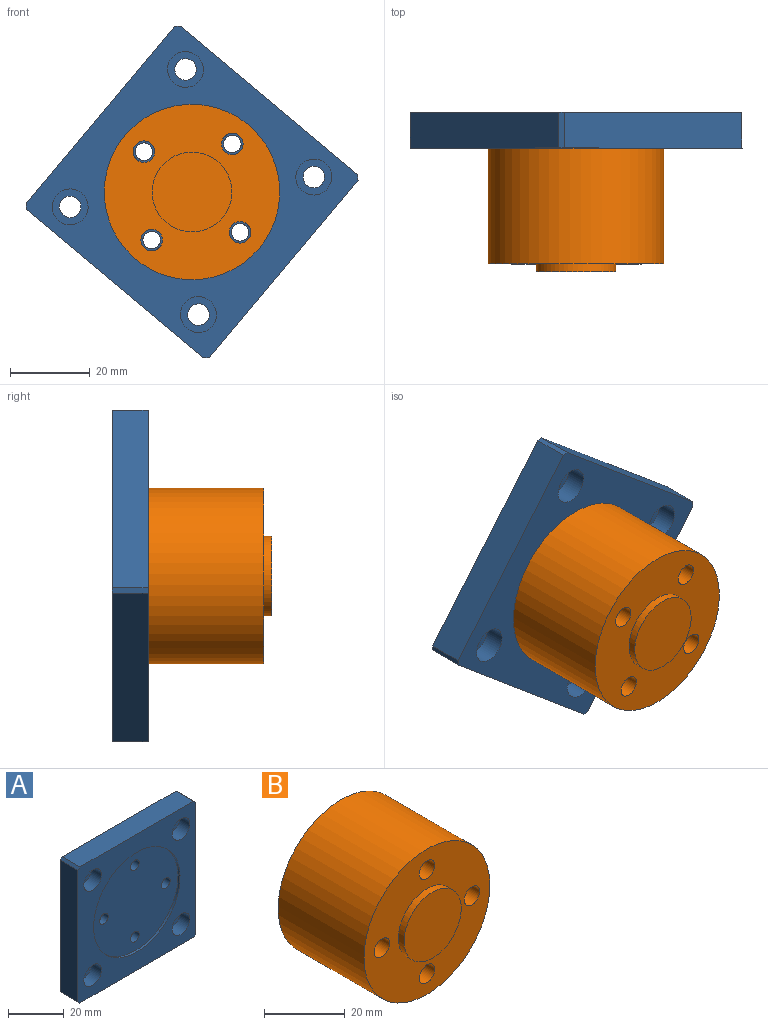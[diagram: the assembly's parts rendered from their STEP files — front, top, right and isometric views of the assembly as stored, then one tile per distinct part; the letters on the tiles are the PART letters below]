
ASSEMBLY  parts=2 mates=1
PART A: 36 faces, bbox 60x9x60 mm
  f0: cylinder r=2.7mm len=5.4mm, axis (0,-1,0), area 64.5mm2, adj f19,f30
  f1: cylinder r=2.7mm len=5.4mm, axis (0,-1,0), area 64.5mm2, adj f19,f28
  f2: cylinder r=2.7mm len=5.4mm, axis (0,-1,0), area 64.5mm2, adj f19,f26
  f3: cylinder r=2.7mm len=5.4mm, axis (0,-1,0), area 64.5mm2, adj f19,f24
  f4: cylinder r=4mm len=8mm, axis (0,1,0), area 105.6mm2, adj f5,f19
  f5: plane 8x8mm, normal (0,1,0), area 35.1mm2, adj f4,f6
  f6: cylinder r=2.2mm len=4.4mm, axis (0,-1,0), area 52.5mm2, adj f5,f21
  f7: cylinder r=4mm len=8mm, axis (0,1,0), area 105.6mm2, adj f8,f19
  f8: plane 8x8mm, normal (0,1,0), area 35.1mm2, adj f7,f9
  f9: cylinder r=2.2mm len=4.4mm, axis (0,-1,0), area 52.5mm2, adj f8,f21
  f10: cylinder r=4mm len=8mm, axis (0,1,0), area 105.6mm2, adj f11,f19
  f11: plane 8x8mm, normal (0,1,0), area 35.1mm2, adj f10,f12
  f12: cylinder r=2.2mm len=4.4mm, axis (0,-1,0), area 52.5mm2, adj f11,f21
  f13: cylinder r=2.2mm len=4.4mm, axis (0,-1,0), area 52.5mm2, adj f21,f22
  f14: plane 58x9mm, normal (-1,0,0), area 522mm2, adj f18,f19,f33,f34
  f15: plane 58x9mm, normal (0,0,-1), area 522mm2, adj f18,f19,f32,f33
  f16: plane 58x9mm, normal (1,0,0), area 522mm2, adj f18,f19,f32,f35
  f17: plane 58x9mm, normal (0,0,1), area 522mm2, adj f18,f19,f34,f35
  f18: plane 60x60mm, normal (0,-1,0), area 1823mm2, adj f14,f15,f16,f17,f20,f25,f27,f29
  f19: plane 60x60mm, normal (0,1,0), area 3305.3mm2, adj f0,f1,f2,f3,f4,f7,f10,f14
  f20: cylinder r=22mm len=44mm, axis (0,-1,0), area 138.2mm2, adj f18,f21
  f21: plane 44x44mm, normal (0,-1,0), area 1459.7mm2, adj f6,f9,f12,f13,f20
  f22: plane 8x8mm, normal (0,1,0), area 35.1mm2, adj f13,f23
  f23: cylinder r=4mm len=8mm, axis (0,1,0), area 105.6mm2, adj f19,f22
  f24: plane 9x9mm, normal (0,-1,0), area 40.7mm2, adj f3,f25
  f25: cylinder r=4.5mm len=9mm, axis (0,-1,0), area 147mm2, adj f18,f24
  f26: plane 9x9mm, normal (0,-1,0), area 40.7mm2, adj f2,f27
  f27: cylinder r=4.5mm len=9mm, axis (0,-1,0), area 147mm2, adj f18,f26
  f28: plane 9x9mm, normal (0,-1,0), area 40.7mm2, adj f1,f29
  f29: cylinder r=4.5mm len=9mm, axis (0,-1,0), area 147mm2, adj f18,f28
  f30: plane 9x9mm, normal (0,-1,0), area 40.7mm2, adj f0,f31
  f31: cylinder r=4.5mm len=9mm, axis (0,-1,0), area 147mm2, adj f18,f30
  f32: plane 9x1mm, normal (0.71,0,-0.71), area 12.7mm2, adj f15,f16,f18,f19
  f33: plane 9x1mm, normal (-0.71,0,-0.71), area 12.7mm2, adj f14,f15,f18,f19
  f34: plane 9x1mm, normal (-0.71,0,0.71), area 12.7mm2, adj f14,f17,f18,f19
  f35: plane 9x1mm, normal (0.71,0,0.71), area 12.7mm2, adj f16,f17,f18,f19
PART B: 17 faces, bbox 44x32x44 mm
  f0: cylinder r=4.5mm len=9mm, axis (0,1,0), area 147mm2, adj f1,f12
  f1: plane 9x9mm, normal (0,1,0), area 40.7mm2, adj f0,f2
  f2: cylinder r=2.7mm len=24.8mm, axis (0,-1,0), area 420.7mm2, adj f1,f11
  f3: cylinder r=4.5mm len=9mm, axis (0,1,0), area 147mm2, adj f4,f12
  f4: plane 9x9mm, normal (0,1,0), area 40.7mm2, adj f3,f5
  f5: cylinder r=2.7mm len=24.8mm, axis (0,-1,0), area 420.7mm2, adj f4,f11
  f6: cylinder r=4.5mm len=9mm, axis (0,1,0), area 147mm2, adj f7,f12
  f7: plane 9x9mm, normal (0,1,0), area 40.7mm2, adj f6,f8
  f8: cylinder r=2.7mm len=24.8mm, axis (0,-1,0), area 420.7mm2, adj f7,f11
  f9: cylinder r=2.7mm len=24.8mm, axis (0,-1,0), area 420.7mm2, adj f11,f15
  f10: cylinder r=22mm len=44mm, axis (0,1,0), area 4146.9mm2, adj f11,f12
  f11: plane 44x44mm, normal (0,-1,0), area 1114.8mm2, adj f2,f5,f8,f9,f10,f13
  f12: plane 44x44mm, normal (0,1,0), area 1266.1mm2, adj f0,f3,f6,f10,f16
  f13: cylinder r=10mm len=20mm, axis (0,1,0), area 125.7mm2, adj f11,f14
  f14: plane 20x20mm, normal (0,-1,0), area 314.2mm2, adj f13
  f15: plane 9x9mm, normal (0,1,0), area 40.7mm2, adj f9,f16
  f16: cylinder r=4.5mm len=9mm, axis (0,1,0), area 147mm2, adj f12,f15
PLACE A rot(axis=(0,-1,0),50deg) t=(-19.2,1,1.6)mm
PLACE B rot(axis=(0,-1,0),50deg) t=(-19.2,-7,1.6)mm
MATE fastened A.f20 <-> B.f13  axis (0,-1,0) through (-19.2,-7,1.6)mm
